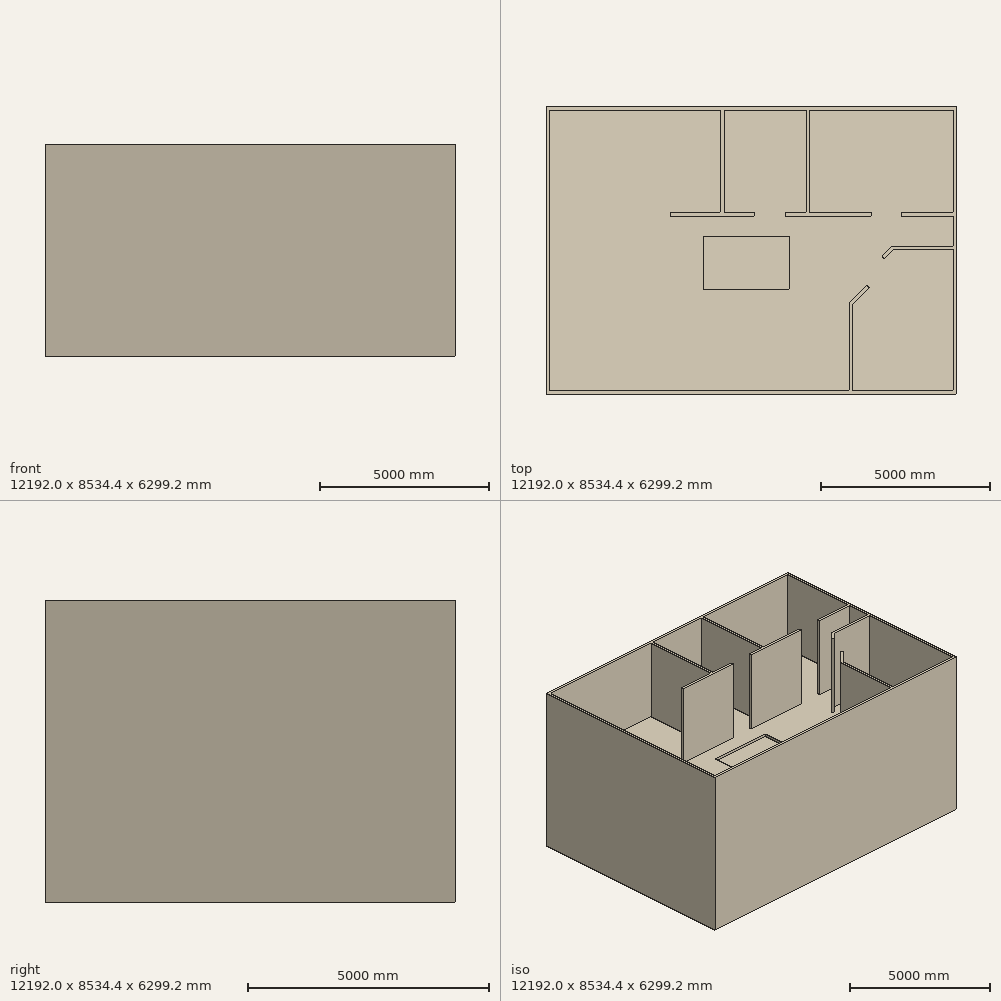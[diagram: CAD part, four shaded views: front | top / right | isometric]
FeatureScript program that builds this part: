
annotation { "Feature Type Name" : "Feature", "Feature Type Description" : "" }
export const myFeature = defineFeature(function(context is Context, id is Id, definition is map)
    precondition{}
    {
        {
            var Q0;
            Q0=qCreatedBy(makeId("Top.planeOp"),FACE);
            var sketch = newSketch(context, id + "F0", { "sketchPlane" : qUnion([Q0])});
            skLineSegment(sketch, "E0.bottom", {"start": v(-6096, 4267.2) * mm, "end": v(6096, 4267.2) * mm});
            skLineSegment(sketch, "E0.top", {"start": v(-6096, -4267.2) * mm, "end": v(6096, -4267.2) * mm});
            skLineSegment(sketch, "E0.left", {"start": v(-6096, 4267.2) * mm, "end": v(-6096, -4267.2) * mm});
            skLineSegment(sketch, "E0.right", {"start": v(6096, 4267.2) * mm, "end": v(6096, -4267.2) * mm});
            skPoint(sketch, "E0.middle", {"position": v(0, 0) * mm});
            skSolve(sketch);
        }
        {
            var Q0;
            Q0 = qSketchRegion(id + "F0", true);
            extrude(context, id + "F1", {"entities" : qUnion([Q0]), "depth" : 101.6 * mm, "offsetDistance" : 25.4 * mm});
        }
        {
            var Q0;
            Q0=makeQuery(id+"F1.opExtrude","CAP_FACE",FACE,{"disambiguationData":[OSD([sQuery(id+"F0.wireOp",EDGE,"E0.bottom"),sQuery(id+"F0.wireOp",EDGE,"E0.top"),sQuery(id+"F0.wireOp",EDGE,"E0.left"),sQuery(id+"F0.wireOp",EDGE,"E0.right")])],"isStart":false});
            var sketch = newSketch(context, id + "F2", { "sketchPlane" : qUnion([Q0])});
            skLineSegment(sketch, "E1.bottom", {"start": v(5994.4, 4165.6) * mm, "end": v(-5994.4, 4165.6) * mm});
            skLineSegment(sketch, "E1.top", {"start": v(5994.4, -4165.6) * mm, "end": v(2184.4, -4165.6) * mm});
            skLineSegment(sketch, "E1.left", {"start": v(5994.4, 4165.6) * mm, "end": v(5994.4, 508) * mm});
            skLineSegment(sketch, "E1.right", {"start": v(-5994.4, 4165.6) * mm, "end": v(-5994.4, 508) * mm});
            skLineSegment(sketch, "E2.bottom", {"start": v(6096, 4267.2) * mm, "end": v(-6096, 4267.2) * mm});
            skLineSegment(sketch, "E2.top", {"start": v(6096, -4267.2) * mm, "end": v(-6096, -4267.2) * mm});
            skLineSegment(sketch, "E2.left", {"start": v(6096, 4267.2) * mm, "end": v(6096, -4267.2) * mm});
            skLineSegment(sketch, "E2.right", {"start": v(-6096, 4267.2) * mm, "end": v(-6096, -4267.2) * mm});
            skLineSegment(sketch, "E3.left", {"start": v(304.8, -4165.6) * mm, "end": v(304.8, -2641.6) * mm});
            skLineSegment(sketch, "E3.right", {"start": v(406.4, -4165.6) * mm, "end": v(406.4, -2683.68) * mm});
            skLineSegment(sketch, "E4.bottom", {"start": v(5994.4, 406.4) * mm, "end": v(2184.4, 406.4) * mm});
            skLineSegment(sketch, "E4.top", {"start": v(5994.4, 508) * mm, "end": v(2184.4, 508) * mm});
            skLineSegment(sketch, "E4.right", {"start": v(2184.4, 406.4) * mm, "end": v(2184.4, 508) * mm});
            skLineSegment(sketch, "E5.left", {"start": v(2082.8, -2133.6) * mm, "end": v(2082.8, -4165.6) * mm});
            skLineSegment(sketch, "E5.right", {"start": v(2184.4, -2032) * mm, "end": v(2184.4, -4165.6) * mm});
            skLineSegment(sketch, "E6.top", {"start": v(-2184.4, -3251.2) * mm, "end": v(-1930.4, -3251.2) * mm});
            skLineSegment(sketch, "E6.left", {"start": v(-2184.4, -4165.6) * mm, "end": v(-2184.4, -3251.2) * mm});
            skLineSegment(sketch, "E6.right", {"start": v(-2082.8, -4165.6) * mm, "end": v(-2082.8, -3352.8) * mm});
            skLineSegment(sketch, "E7.bottom", {"start": v(-1320.8, -3251.2) * mm, "end": v(-1066.8, -3251.2) * mm});
            skLineSegment(sketch, "E7.left", {"start": v(-1168.4, -3352.8) * mm, "end": v(-1168.4, -4165.6) * mm});
            skLineSegment(sketch, "E7.right", {"start": v(-1066.8, -3251.2) * mm, "end": v(-1066.8, -4165.6) * mm});
            skLineSegment(sketch, "E8.bottom", {"start": v(-5994.4, 508) * mm, "end": v(-3251.2, 508) * mm});
            skLineSegment(sketch, "E8.top", {"start": v(-5994.4, 406.4) * mm, "end": v(-3251.2, 406.4) * mm});
            skLineSegment(sketch, "E8.right", {"start": v(-3251.2, 508) * mm, "end": v(-3251.2, 406.4) * mm});
            skLineSegment(sketch, "E9", {"start": v(-2082.8, -3352.8) * mm, "end": v(-1930.4, -3352.8) * mm});
            skLineSegment(sketch, "E10", {"start": v(-1930.4, -3352.8) * mm, "end": v(-1930.4, -3251.2) * mm});
            skLineSegment(sketch, "E11", {"start": v(-1168.4, -3352.8) * mm, "end": v(-1320.8, -3352.8) * mm});
            skLineSegment(sketch, "E12", {"start": v(-1320.8, -3352.8) * mm, "end": v(-1320.8, -3251.2) * mm});
            skLineSegment(sketch, "E13.trimOffspring", {"start": v(-5994.4, 406.4) * mm, "end": v(-5994.4, -4165.6) * mm});
            skLineSegment(sketch, "E14.trimOffspring", {"start": v(-2184.4, -4165.6) * mm, "end": v(-5994.4, -4165.6) * mm});
            skLineSegment(sketch, "E15.trimOffspring", {"start": v(-1168.4, -4165.6) * mm, "end": v(-2082.8, -4165.6) * mm});
            skLineSegment(sketch, "E16.trimOffspring", {"start": v(5994.4, 406.4) * mm, "end": v(5994.4, -4165.6) * mm});
            skLineSegment(sketch, "E17.trimOffspring", {"start": v(304.8, -4165.6) * mm, "end": v(-1066.8, -4165.6) * mm});
            skLineSegment(sketch, "E18.trimOffspring", {"start": v(2082.8, -4165.6) * mm, "end": v(406.4, -4165.6) * mm});
            skLineSegment(sketch, "E19", {"start": v(304.8, -2641.6) * mm, "end": v(914.4, -2032) * mm});
            skLineSegment(sketch, "E20", {"start": v(406.4, -2683.68) * mm, "end": v(956.48, -2133.6) * mm});
            skLineSegment(sketch, "E21", {"start": v(914.4, -2032) * mm, "end": v(1092.2, -2032) * mm});
            skLineSegment(sketch, "E22", {"start": v(1092.2, -2032) * mm, "end": v(1092.2, -2133.6) * mm});
            skLineSegment(sketch, "E23", {"start": v(956.48, -2133.6) * mm, "end": v(1092.2, -2133.6) * mm});
            skLineSegment(sketch, "E24", {"start": v(2082.8, -2133.6) * mm, "end": v(2006.6, -2133.6) * mm});
            skLineSegment(sketch, "E25", {"start": v(2006.6, -2133.6) * mm, "end": v(2006.6, -2032) * mm});
            skLineSegment(sketch, "E26", {"start": v(2184.4, -2032) * mm, "end": v(2006.6, -2032) * mm});
            skSolve(sketch);
        }
        {
            var Q0;
            Q0 = qSketchRegion(id + "F2", true);
            extrude(context, id + "F3", {"entities" : qUnion([Q0]), "operationType" : NewBodyOperationType.ADD, "depth" : 3048 * mm, "offsetDistance" : 25.4 * mm});
        }
        {
            var Q0;
            Q0=makeQuery(id+"F3.opExtrude","CAP_FACE",FACE,{"disambiguationData":[OSD([sQuery(id+"F2.wireOp",EDGE,"E1.bottom"),sQuery(id+"F2.wireOp",EDGE,"E1.top"),sQuery(id+"F2.wireOp",EDGE,"E1.left"),sQuery(id+"F2.wireOp",EDGE,"E1.right"),sQuery(id+"F2.wireOp",EDGE,"E2.bottom"),sQuery(id+"F2.wireOp",EDGE,"E2.top"),sQuery(id+"F2.wireOp",EDGE,"E2.left"),sQuery(id+"F2.wireOp",EDGE,"E2.right"),sQuery(id+"F2.wireOp",EDGE,"E3.left"),sQuery(id+"F2.wireOp",EDGE,"E3.right"),sQuery(id+"F2.wireOp",EDGE,"E4.bottom"),sQuery(id+"F2.wireOp",EDGE,"E4.top"),sQuery(id+"F2.wireOp",EDGE,"E4.right"),sQuery(id+"F2.wireOp",EDGE,"E5.left"),sQuery(id+"F2.wireOp",EDGE,"E5.right"),sQuery(id+"F2.wireOp",EDGE,"E6.top"),sQuery(id+"F2.wireOp",EDGE,"E6.left"),sQuery(id+"F2.wireOp",EDGE,"E6.right"),sQuery(id+"F2.wireOp",EDGE,"E7.bottom"),sQuery(id+"F2.wireOp",EDGE,"E7.left"),sQuery(id+"F2.wireOp",EDGE,"E7.right"),sQuery(id+"F2.wireOp",EDGE,"E8.bottom"),sQuery(id+"F2.wireOp",EDGE,"E8.top"),sQuery(id+"F2.wireOp",EDGE,"E8.right"),sQuery(id+"F2.wireOp",EDGE,"E9"),sQuery(id+"F2.wireOp",EDGE,"E10"),sQuery(id+"F2.wireOp",EDGE,"E11"),sQuery(id+"F2.wireOp",EDGE,"E12"),sQuery(id+"F2.wireOp",EDGE,"E13.trimOffspring"),sQuery(id+"F2.wireOp",EDGE,"E14.trimOffspring"),sQuery(id+"F2.wireOp",EDGE,"E15.trimOffspring"),sQuery(id+"F2.wireOp",EDGE,"E16.trimOffspring"),sQuery(id+"F2.wireOp",EDGE,"E17.trimOffspring"),sQuery(id+"F2.wireOp",EDGE,"E18.trimOffspring"),sQuery(id+"F2.wireOp",EDGE,"E19"),sQuery(id+"F2.wireOp",EDGE,"E20"),sQuery(id+"F2.wireOp",EDGE,"E21"),sQuery(id+"F2.wireOp",EDGE,"E22"),sQuery(id+"F2.wireOp",EDGE,"E23"),sQuery(id+"F2.wireOp",EDGE,"E24"),sQuery(id+"F2.wireOp",EDGE,"E25"),sQuery(id+"F2.wireOp",EDGE,"E26")])],"isStart":false});
            var sketch = newSketch(context, id + "F4", { "sketchPlane" : qUnion([Q0])});
            skLineSegment(sketch, "E27.bottom", {"start": v(-6096, 4267.2) * mm, "end": v(6096, 4267.2) * mm});
            skLineSegment(sketch, "E27.top", {"start": v(-6096, -4267.2) * mm, "end": v(6096, -4267.2) * mm});
            skLineSegment(sketch, "E27.left", {"start": v(-6096, 4267.2) * mm, "end": v(-6096, -4267.2) * mm});
            skLineSegment(sketch, "E27.right", {"start": v(6096, 4267.2) * mm, "end": v(6096, -4267.2) * mm});
            skLineSegment(sketch, "E28.bottom", {"start": v(-1422.4, 406.4) * mm, "end": v(1117.6, 406.4) * mm});
            skLineSegment(sketch, "E28.top", {"start": v(-1422.4, -1156.96) * mm, "end": v(1117.6, -1156.96) * mm});
            skLineSegment(sketch, "E28.left", {"start": v(-1422.4, 406.4) * mm, "end": v(-1422.4, -1156.96) * mm});
            skLineSegment(sketch, "E28.right", {"start": v(1117.6, 406.4) * mm, "end": v(1117.6, -1156.96) * mm});
            skSolve(sketch);
        }
        {
            var Q0;
            Q0 = qSketchRegion(id + "F4", true);
            extrude(context, id + "F5", {"entities" : qUnion([Q0]), "operationType" : NewBodyOperationType.ADD, "depth" : 101.6 * mm, "offsetDistance" : 25.4 * mm});
        }
        {
            var Q0;
            Q0=makeQuery(id+"F5.opExtrude","CAP_FACE",FACE,{"disambiguationData":[OSD([sQuery(id+"F4.wireOp",EDGE,"E27.bottom"),sQuery(id+"F4.wireOp",EDGE,"E27.top"),sQuery(id+"F4.wireOp",EDGE,"E27.left"),sQuery(id+"F4.wireOp",EDGE,"E27.right"),sQuery(id+"F4.wireOp",EDGE,"E28.bottom"),sQuery(id+"F4.wireOp",EDGE,"E28.top"),sQuery(id+"F4.wireOp",EDGE,"E28.left"),sQuery(id+"F4.wireOp",EDGE,"E28.right")])],"isStart":false});
            var sketch = newSketch(context, id + "F6", { "sketchPlane" : qUnion([Q0])});
            skLineSegment(sketch, "E29.bottom", {"start": v(6096, 4267.2) * mm, "end": v(-6096, 4267.2) * mm});
            skLineSegment(sketch, "E29.top", {"start": v(6096, -4267.2) * mm, "end": v(-6096, -4267.2) * mm});
            skLineSegment(sketch, "E29.left", {"start": v(6096, 4267.2) * mm, "end": v(6096, -4267.2) * mm});
            skLineSegment(sketch, "E29.right", {"start": v(-6096, 4267.2) * mm, "end": v(-6096, -4267.2) * mm});
            skLineSegment(sketch, "E30.bottom", {"start": v(-5994.4, -4165.6) * mm, "end": v(2902.66, -4165.6) * mm});
            skLineSegment(sketch, "E30.top", {"start": v(-5994.4, 4165.6) * mm, "end": v(-914.4, 4165.6) * mm});
            skLineSegment(sketch, "E30.left", {"start": v(-5994.4, -4165.6) * mm, "end": v(-5994.4, 4165.6) * mm});
            skLineSegment(sketch, "E30.right", {"start": v(5994.4, -4165.6) * mm, "end": v(5994.4, 21.37) * mm});
            skLineSegment(sketch, "E31", {"start": v(2902.66, -4165.6) * mm, "end": v(2902.66, -1579.93) * mm});
            skLineSegment(sketch, "E32", {"start": v(2902.66, -1579.93) * mm, "end": v(3438.55, -1044.04) * mm});
            skLineSegment(sketch, "E33", {"start": v(3438.55, -1044.04) * mm, "end": v(3510.4, -1115.88) * mm});
            skLineSegment(sketch, "E34", {"start": v(3510.4, -1115.88) * mm, "end": v(3004.26, -1622.02) * mm});
            skLineSegment(sketch, "E35", {"start": v(3004.26, -1622.02) * mm, "end": v(3004.26, -4165.6) * mm});
            skLineSegment(sketch, "E36", {"start": v(3875.05, -187.38) * mm, "end": v(4185.4, 122.97) * mm});
            skLineSegment(sketch, "E37", {"start": v(4185.4, 122.97) * mm, "end": v(5994.4, 122.97) * mm});
            skLineSegment(sketch, "E38", {"start": v(5994.4, 21.37) * mm, "end": v(4227.48, 21.37) * mm});
            skLineSegment(sketch, "E39", {"start": v(4227.48, 21.37) * mm, "end": v(3946.9, -259.22) * mm});
            skLineSegment(sketch, "E40", {"start": v(3946.9, -259.22) * mm, "end": v(3875.05, -187.38) * mm});
            skLineSegment(sketch, "E41", {"start": v(1016, 1016) * mm, "end": v(3556, 1016) * mm});
            skLineSegment(sketch, "E42", {"start": v(3556, 1016) * mm, "end": v(3556, 1117.6) * mm});
            skLineSegment(sketch, "E43", {"start": v(3556, 1117.6) * mm, "end": v(1727.2, 1117.6) * mm});
            skLineSegment(sketch, "E44", {"start": v(1727.2, 1117.6) * mm, "end": v(1727.2, 4165.6) * mm});
            skLineSegment(sketch, "E45", {"start": v(4470.4, 1117.6) * mm, "end": v(4470.4, 1016) * mm});
            skLineSegment(sketch, "E46", {"start": v(4470.4, 1016) * mm, "end": v(5994.4, 1016) * mm});
            skLineSegment(sketch, "E47", {"start": v(4470.4, 1117.6) * mm, "end": v(5994.4, 1117.6) * mm});
            skPoint(sketch, "E48.end.orphan", {"position": v(4470.4, 3474.16) * mm});
            skLineSegment(sketch, "E49.trimOffspring", {"start": v(1727.2, 4165.6) * mm, "end": v(5994.4, 4165.6) * mm});
            skLineSegment(sketch, "E50.trimOffspring", {"start": v(5994.4, 1117.6) * mm, "end": v(5994.4, 4165.6) * mm});
            skLineSegment(sketch, "E51.trimOffspring", {"start": v(5994.4, 122.97) * mm, "end": v(5994.4, 1016) * mm});
            skLineSegment(sketch, "E52.trimOffspring", {"start": v(3004.26, -4165.6) * mm, "end": v(5994.4, -4165.6) * mm});
            skLineSegment(sketch, "E53", {"start": v(1625.6, 4165.6) * mm, "end": v(1625.6, 1117.6) * mm});
            skLineSegment(sketch, "E54", {"start": v(1625.6, 1117.6) * mm, "end": v(1016, 1117.6) * mm});
            skLineSegment(sketch, "E55", {"start": v(1016, 1117.6) * mm, "end": v(1016, 1016) * mm});
            skLineSegment(sketch, "E56", {"start": v(-812.8, 4165.6) * mm, "end": v(-812.8, 1117.6) * mm});
            skLineSegment(sketch, "E57", {"start": v(-812.8, 1117.6) * mm, "end": v(101.6, 1117.6) * mm});
            skLineSegment(sketch, "E58", {"start": v(101.6, 1117.6) * mm, "end": v(101.6, 1016) * mm});
            skLineSegment(sketch, "E59", {"start": v(101.6, 1016) * mm, "end": v(-2406.57, 1016) * mm});
            skLineSegment(sketch, "E60", {"start": v(-2406.57, 1016) * mm, "end": v(-2406.57, 1117.6) * mm});
            skLineSegment(sketch, "E61", {"start": v(-2406.57, 1117.6) * mm, "end": v(-914.4, 1117.6) * mm});
            skLineSegment(sketch, "E62", {"start": v(-914.4, 1117.6) * mm, "end": v(-914.4, 4165.6) * mm});
            skLineSegment(sketch, "E63.trimOffspring", {"start": v(-812.8, 4165.6) * mm, "end": v(1625.6, 4165.6) * mm});
            skSolve(sketch);
        }
        {
            var Q0;
            Q0 = qSketchRegion(id + "F6", true);
            extrude(context, id + "F7", {"entities" : qUnion([Q0]), "operationType" : NewBodyOperationType.ADD, "depth" : 3048 * mm, "offsetDistance" : 25.4 * mm});
        }
    });
